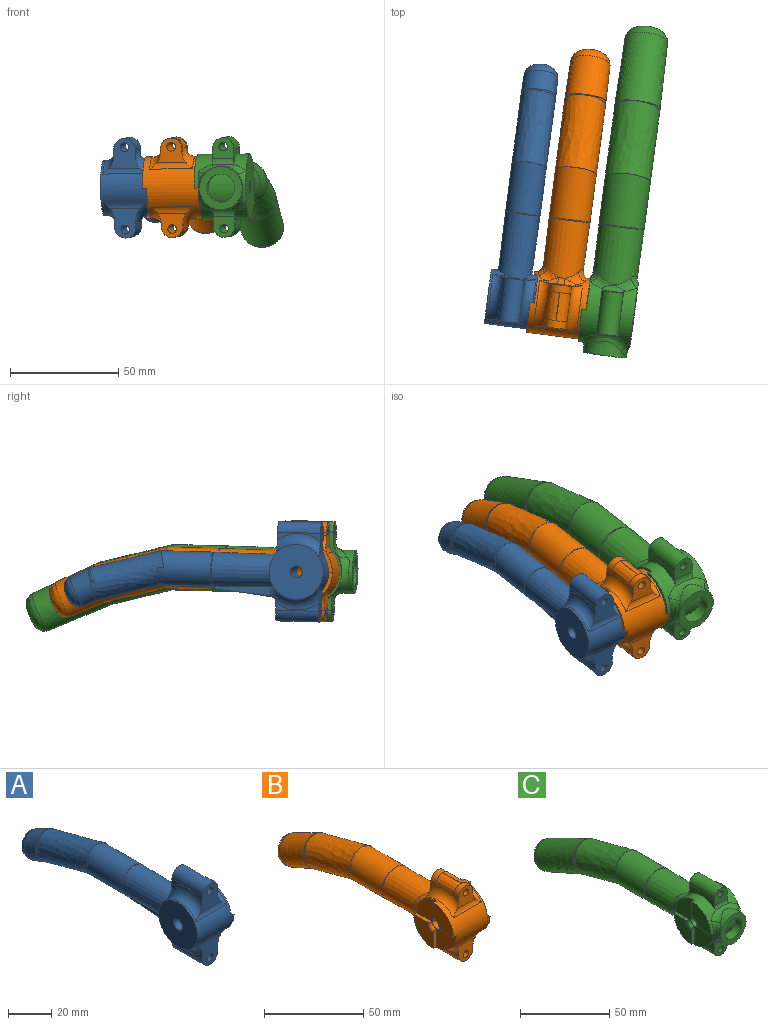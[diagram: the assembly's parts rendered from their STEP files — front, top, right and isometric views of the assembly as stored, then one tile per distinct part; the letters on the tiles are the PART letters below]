
ASSEMBLY  parts=3 mates=2
PART A: 65 faces, bbox 29.9x133.2x48.8 mm
  f0: plane 12.65x12.65mm, normal (1,0,0), area 119.5mm2, adj f1,f9,f11,f12
  f1: plane 9.85x2mm, normal (0,-1,0), area 18.8mm2, adj f0,f2,f8,f12
  f2: plane 12.65x12.65mm, normal (1,0,0), area 107.6mm2, adj f1,f3,f8,f12
  f3: plane 9.85x2mm, normal (0,0,-1), area 18.8mm2, adj f2,f4,f8,f12
  f4: plane 12.65x12.65mm, normal (1,0,0), area 119.5mm2, adj f3,f5,f9,f12
  f5: plane 9.85x2mm, normal (0,1,0), area 18.8mm2, adj f4,f6,f7,f12
  f6: plane 12.65x12.65mm, normal (1,0,0), area 107.6mm2, adj f5,f7,f11,f12
  f7: torus R=4.8mm, axis (1,0,0), area 17.4mm2, adj f5,f6,f9,f11
  f8: torus R=4.8mm, axis (1,0,0), area 17.4mm2, adj f1,f2,f3,f9
  f9: cylinder r=2.8mm len=22mm, axis (1,0,0), area 387mm2, adj f0,f4,f7,f8,f10
  f10: plane 25.3x25.3mm, normal (-1,0,0), area 478.1mm2, adj f9,f12
  f11: plane 9.85x2mm, normal (0,0,1), area 18.8mm2, adj f0,f6,f7,f12
  f12: cylinder r=12.65mm len=25.3mm, axis (-1,0,0), area 626.3mm2, adj f0,f1,f2,f3,f4,f5,f6,f10
  f13: torus R=17.65mm, axis (1,0,0), area 177.5mm2, adj f12,f14,f18,f19,f20,f22
  f14: plane 15.43x14.51mm, normal (0,1,0), area 128.9mm2, adj f13,f15,f16,f17,f19,f21,f22
  f15: plane 20x3.46mm, normal (1,0,0), area 26.9mm2, adj f14,f16,f18,f21
  f16: cylinder r=5mm len=20mm, axis (0,1,0), area 314.2mm2, adj f14,f15,f18,f19
  f17: cylinder r=2mm len=20mm, axis (0,1,0), area 251.3mm2, adj f14,f18
  f18: plane 14.2x13.92mm, normal (0,-1,0), area 120.3mm2, adj f13,f15,f16,f17,f19,f20,f21
  f19: plane 20x3.46mm, normal (-1,0,0), area 26.9mm2, adj f13,f14,f16,f18
  f20: cylinder r=5mm len=20mm, axis (-1,0,0), area 47.2mm2, adj f12,f13,f18,f21
  f21: torus R=17.65mm, axis (1,0,0), area 177.5mm2, adj f12,f14,f15,f18,f20,f22
  f22: cylinder r=3mm len=20mm, axis (-1,0,0), area 27.8mm2, adj f12,f13,f14,f21,f43
  f23: cylinder r=3mm len=7.15mm, axis (0,0,-1), area 23.7mm2, adj f12,f24,f25,f32,f35,f36,f37,f43
  f24: plane 3.09x2.1mm, normal (0,1,0), area 2.6mm2, adj f23,f36,f37
  f25: cylinder r=3mm len=10.04mm, axis (-1,0,0), area 32.2mm2, adj f23,f26,f32,f37,f39,f42
  f26: plane 10x8.54mm, normal (0,1,0), area 62.1mm2, adj f25,f27,f29,f30,f31,f37,f39
  f27: plane 20x3.46mm, normal (-1,0,0), area 26.9mm2, adj f26,f28,f29,f39
  f28: plane 13.98x13.7mm, normal (0,-1,0), area 120.3mm2, adj f27,f29,f30,f31,f37,f38,f39
  f29: cylinder r=5mm len=20mm, axis (0,-1,0), area 314.2mm2, adj f26,f27,f28,f30
  f30: plane 20x3.46mm, normal (1,0,0), area 26.9mm2, adj f26,f28,f29,f37
  f31: cylinder r=2mm len=20mm, axis (0,1,0), area 251.3mm2, adj f26,f28
  f32: plane 27.33x5.03mm, normal (0,0.09,-1), area 137.3mm2, adj f23,f25,f33,f34,f35,f42
  f33: plane 6.3x3.44mm, normal (0,0.53,0.85), area 10.1mm2, adj f32,f34,f35,f43
  f34: plane 27.05x4.1mm, normal (-1,0,0), area 71.9mm2, adj f32,f33,f42,f43
  f35: plane 27.05x4.1mm, normal (1,0,0), area 71.9mm2, adj f23,f32,f33,f43
  f36: cylinder r=3mm len=6.17mm, axis (-1,0,0), area 7.3mm2, adj f12,f23,f24,f37
  f37: torus R=17.65mm, axis (1,0,0), area 176.7mm2, adj f12,f23,f24,f25,f26,f28,f30,f36
  f38: cylinder r=5mm len=20mm, axis (-1,0,0), area 47.2mm2, adj f12,f28,f37,f39
  f39: torus R=17.65mm, axis (1,0,0), area 176.7mm2, adj f12,f25,f26,f27,f28,f38,f40,f41
  f40: plane 3.1x2.11mm, normal (0,1,0), area 2.6mm2, adj f39,f41,f42
  f41: cylinder r=3mm len=6.17mm, axis (-1,0,0), area 7.3mm2, adj f12,f39,f40,f42
  f42: cylinder r=3mm len=7.15mm, axis (0,0,1), area 23.7mm2, adj f12,f25,f32,f34,f39,f40,f41,f43
  f43: cone r=8mm half-angle=0.5deg, axis (0,1,0), area 1269.4mm2, adj f12,f22,f23,f33,f34,f35,f42,f44
  f44: revolved ~16x16mm, area 43.9mm2, adj f43,f45
  f45: cylinder r=8mm len=24.78mm, axis (0,-1,0), area 1203.2mm2, adj f44,f46,f53,f54
  f46: extruded ~37.81x23.99mm, area 1582mm2, adj f45,f47,f48,f49,f53,f54
  f47: bspline ~16x7.05mm, area 0mm2, adj f46,f48
  f48: plane 18.67x9.72mm, normal (0,-0.91,0.42), area 2.5mm2, adj f46,f47
  f49: plane 18.66x17.58mm, normal (0,0.97,-0.26), area 1.8mm2, adj f46,f50
  f50: bspline ~17.04x15.92mm, area 394.6mm2, adj f49,f51
  f51: bspline ~15.65x15.49mm, area 282.7mm2, adj f50,f52
  f52: plane 5.65x4.42mm, normal (0,0.91,-0.42), area 21.5mm2, adj f51
  f53: plane 16x7.84mm, normal (0,-0.97,0.26), area 5.9mm2, adj f45,f46,f54
  f54: extruded ~3x1.15mm, area 0.6mm2, adj f45,f46,f53
  f55: cylinder r=12.65mm len=7.98mm, axis (-1,0,0), area 15.7mm2, adj f59,f61,f62,f63
  f56: plane 8x7.11mm, normal (0,0.91,-0.42), area 49.3mm2, adj f58
  f57: plane 10.36x6.76mm, normal (0,0.97,-0.26), area 8.2mm2, adj f58,f59
  f58: extruded ~34.57x16.19mm, area 786.2mm2, adj f56,f57,f59,f60
  f59: cylinder r=4mm len=52.79mm, axis (0,1,0), area 1145.8mm2, adj f55,f57,f58,f60,f61,f62,f63,f64
  f60: cylinder r=4mm len=3mm, axis (0,1,0), area 0.6mm2, adj f58,f59
  f61: plane 5x2.16mm, normal (0,0.42,-0.91), area 8.7mm2, adj f55,f59,f62,f63
  f62: plane 18.53x6.25mm, normal (1,0,0), area 82.9mm2, adj f55,f59,f61,f64
  f63: plane 18.53x6.25mm, normal (-1,0,0), area 82.9mm2, adj f55,f59,f61,f64
  f64: plane 15.59x10.81mm, normal (0,-0.53,-0.85), area 70.2mm2, adj f59,f62,f63
PART B: 89 faces, bbox 30.3x142.9x53.6 mm
  f0: plane 14.71x14.71mm, normal (-1,0,0), area 151.1mm2, adj f1,f75,f76,f77,f78
  f1: cylinder r=14.15mm len=28.3mm, axis (-1,0,0), area 732mm2, adj f0,f2,f34,f35,f36,f37,f38,f40
  f2: cylinder r=5mm len=20mm, axis (-1,0,0), area 55.5mm2, adj f1,f3,f34,f74
  f3: plane 13.2x11.23mm, normal (0,-1,0), area 92mm2, adj f2,f4,f5,f32,f33,f34,f74
  f4: plane 3.46x1.67mm, normal (-1,0,0), area 2.6mm2, adj f3,f5,f74
  f5: cylinder r=5mm len=10mm, axis (0,1,0), area 54.4mm2, adj f3,f4,f6,f31,f32
  f6: bspline ~18.4x5.66mm, area 97.7mm2, adj f5,f7,f8,f74
  f7: plane 13.07x0.13mm, normal (0,0,1), area 0.9mm2, adj f6,f31
  f8: cylinder r=5mm len=10mm, axis (0,1,0), area 54.4mm2, adj f6,f9,f10,f11,f31
  f9: plane 3.46x1.67mm, normal (1,0,0), area 2.6mm2, adj f8,f11,f34
  f10: plane 3.46x1.67mm, normal (-1,0,0), area 2.6mm2, adj f8,f11,f74
  f11: plane 14.55x11.95mm, normal (0,1,0), area 93.7mm2, adj f8,f9,f10,f12,f13,f30,f33,f34
  f12: bspline ~6.48x3.42mm, area 18.4mm2, adj f11,f13,f72,f73
  f13: torus R=12.26mm, axis (0,1,0), area 15.9mm2, adj f11,f12,f14,f30
  f14: cone r=9.5mm half-angle=0.5deg, axis (0,1,0), area 1289.9mm2, adj f13,f15,f17,f18,f19,f36,f37,f48
  f15: plane 28.43x6.7mm, normal (1,0,0), area 56.4mm2, adj f14,f16,f18,f48,f63
  f16: cylinder r=3mm len=5mm, axis (-1,0,0), area 21.6mm2, adj f15,f17,f18,f63
  f17: plane 28.43x6.69mm, normal (-1,0,0), area 56.4mm2, adj f14,f16,f18,f63,f64
  f18: plane 25.69x5mm, normal (0,0.13,-0.99), area 121.5mm2, adj f14,f15,f16,f17
  f19: revolved ~19x19mm, area 52.1mm2, adj f14,f20
  f20: cylinder r=9.5mm len=24.78mm, axis (0,-1,0), area 1436.2mm2, adj f19,f21,f28,f29
  f21: extruded ~38.56x26.79mm, area 1900.1mm2, adj f20,f22,f23,f24,f28,f29
  f22: bspline ~19x8.34mm, area 0mm2, adj f21,f23
  f23: plane 19.26x8.6mm, normal (0,-0.91,0.42), area 2.3mm2, adj f21,f22
  f24: plane 22.16x20.88mm, normal (0,0.97,-0.26), area 2.2mm2, adj f21,f25
  f25: bspline ~23.93x23.7mm, area 1035.6mm2, adj f24,f26
  f26: bspline ~18.31x17.75mm, area 345.6mm2, adj f25,f27
  f27: plane 8.3x6.69mm, normal (0,0.91,-0.42), area 48mm2, adj f26
  f28: plane 19x9.24mm, normal (0,-0.97,0.26), area 5.4mm2, adj f20,f21,f29
  f29: extruded ~3x1.15mm, area 0.6mm2, adj f20,f21,f28
  f30: bspline ~6.35x3.35mm, area 18.4mm2, adj f11,f13,f35,f36
  f31: bspline ~18.4x5.66mm, area 97.7mm2, adj f5,f7,f8,f34
  f32: plane 3.46x1.67mm, normal (1,0,0), area 2.6mm2, adj f3,f5,f34
  f33: cylinder r=2mm len=20mm, axis (0,1,0), area 251.3mm2, adj f3,f11
  f34: torus R=19.15mm, axis (1,0,0), area 174.3mm2, adj f1,f2,f3,f9,f11,f31,f32,f35
  f35: cylinder r=3mm len=3.08mm, axis (-1,0,0), area 3.6mm2, adj f1,f11,f30,f34
  f36: bspline ~11.34x7.93mm, area 33.4mm2, adj f1,f14,f30,f37
  f37: bspline ~15.66x6.2mm, area 62.8mm2, adj f1,f14,f36,f47,f48
  f38: plane 11.35x2mm, normal (0,0,-1), area 21.8mm2, adj f1,f39,f40,f47
  f39: torus R=4.8mm, axis (1,0,0), area 17.4mm2, adj f38,f40,f41,f76
  f40: plane 14.15x14.15mm, normal (1,0,0), area 139.2mm2, adj f1,f38,f39,f41
  f41: plane 11.35x2mm, normal (0,-1,0), area 21.8mm2, adj f1,f39,f40,f42
  f42: plane 14.15x14.15mm, normal (1,0,0), area 151.1mm2, adj f1,f41,f43,f76
  f43: plane 11.35x2mm, normal (0,0,1), area 21.8mm2, adj f1,f42,f44,f45
  f44: torus R=4.8mm, axis (1,0,0), area 17.4mm2, adj f43,f45,f46,f76
  f45: plane 14.15x14.15mm, normal (1,0,0), area 139.2mm2, adj f1,f43,f44,f46
  f46: plane 11.35x2mm, normal (0,1,0), area 21.8mm2, adj f1,f44,f45,f47
  f47: plane 14.71x14.71mm, normal (1,0,0), area 151.1mm2, adj f1,f37,f38,f46,f76
  f48: bspline ~9.3x7.24mm, area 39.3mm2, adj f1,f14,f15,f37,f63
  f49: torus R=19.15mm, axis (1,0,0), area 170.7mm2, adj f1,f50,f57,f58,f59,f61,f63
  f50: plane 3.46x1.67mm, normal (1,0,0), area 2.6mm2, adj f49,f51,f59
  f51: cylinder r=5mm len=10mm, axis (0,-1,0), area 54.4mm2, adj f50,f52,f56,f57,f59
  f52: bspline ~18.4x5.66mm, area 97.7mm2, adj f51,f53,f54,f62
  f53: plane 13.07x0.13mm, normal (0,0,-1), area 0.9mm2, adj f52,f57
  f54: cylinder r=5mm len=10mm, axis (0,-1,0), area 54.4mm2, adj f52,f55,f57,f58,f63
  f55: plane 3.46x1.67mm, normal (-1,0,0), area 2.6mm2, adj f54,f62,f63
  f56: plane 3.46x1.67mm, normal (-1,0,0), area 2.6mm2, adj f51,f59,f62
  f57: bspline ~18.4x5.66mm, area 97.7mm2, adj f49,f51,f53,f54
  f58: plane 3.46x1.67mm, normal (1,0,0), area 2.6mm2, adj f49,f54,f63
  f59: plane 13.2x11.23mm, normal (0,-1,0), area 92mm2, adj f49,f50,f51,f56,f60,f61,f62
  f60: cylinder r=2mm len=20mm, axis (0,1,0), area 251.3mm2, adj f59,f63
  f61: cylinder r=5mm len=20mm, axis (-1,0,0), area 55.5mm2, adj f1,f49,f59,f62
  f62: torus R=19.15mm, axis (1,0,0), area 170.7mm2, adj f1,f52,f55,f56,f59,f61,f63
  f63: plane 20.93x13.92mm, normal (0,1,0), area 93.4mm2, adj f1,f15,f16,f17,f48,f49,f54,f55
  f64: bspline ~11.02x8.01mm, area 39.3mm2, adj f1,f14,f17,f63,f78
  f65: plane 14.15x14.15mm, normal (-1,0,0), area 139.2mm2, adj f1,f66,f67,f77
  f66: torus R=4.8mm, axis (-1,0,0), area 17.4mm2, adj f65,f67,f76,f77
  f67: plane 11.35x2mm, normal (0,-1,0), area 21.8mm2, adj f1,f65,f66,f68
  f68: plane 14.15x14.15mm, normal (-1,0,0), area 151.1mm2, adj f1,f67,f69,f76
  f69: plane 11.35x2mm, normal (0,0,-1), area 21.8mm2, adj f1,f68,f70,f71
  f70: torus R=4.8mm, axis (-1,0,0), area 17.4mm2, adj f69,f71,f75,f76
  f71: plane 14.15x14.15mm, normal (-1,0,0), area 139.2mm2, adj f1,f69,f70,f75
  f72: bspline ~11.05x8mm, area 33.4mm2, adj f1,f12,f14,f78
  f73: cylinder r=3mm len=3.08mm, axis (-1,0,0), area 3.6mm2, adj f1,f11,f12,f74
  f74: torus R=19.15mm, axis (1,0,0), area 174.3mm2, adj f1,f2,f3,f4,f6,f10,f11,f73
  f75: plane 11.35x2mm, normal (0,1,0), area 21.8mm2, adj f0,f1,f70,f71
  f76: cylinder r=2.8mm len=22mm, axis (1,0,0), area 387mm2, adj f0,f39,f42,f44,f47,f66,f68,f70
  f77: plane 11.35x2mm, normal (0,0,1), area 21.8mm2, adj f0,f1,f65,f66
  f78: bspline ~15.66x6.2mm, area 62.8mm2, adj f0,f1,f14,f64,f72
  f79: cylinder r=5.5mm len=52.02mm, axis (0,1,0), area 1595.4mm2, adj f80,f81,f83,f84,f85,f86,f87,f88
  f80: cylinder r=5.5mm len=3mm, axis (0,1,0), area 0.6mm2, adj f79,f84
  f81: cylinder r=14.15mm len=10.99mm, axis (-1,0,0), area 47.6mm2, adj f79,f85,f86,f87
  f82: plane 11x9.78mm, normal (0,0.91,-0.42), area 93.2mm2, adj f84
  f83: plane 11x5.9mm, normal (0,0.97,-0.26), area 12.1mm2, adj f79,f84
  f84: extruded ~35.57x19.06mm, area 1085.7mm2, adj f79,f80,f82,f83
  f85: plane 5.13x3.74mm, normal (0,0.42,-0.91), area 18.9mm2, adj f79,f81,f86,f87,f88
  f86: plane 20.35x9.8mm, normal (1,0,0), area 115mm2, adj f79,f81,f85,f88
  f87: plane 20.35x9.8mm, normal (-1,0,0), area 115mm2, adj f79,f81,f85,f88
  f88: plane 17.41x10.93mm, normal (0,-0.53,-0.85), area 99.4mm2, adj f79,f85,f86,f87
PART C: 74 faces, bbox 28.8x158x59.5 mm
  f0: cylinder r=15.15mm len=25.94mm, axis (-1,0,0), area 164.5mm2, adj f1,f61,f62,f63
  f1: bspline ~23.08x7.77mm, area 88.7mm2, adj f0,f2,f8,f9,f55,f56,f60,f61
  f2: cylinder r=5mm len=10mm, axis (-1,0,0), area 29.8mm2, adj f1,f3,f8,f61
  f3: plane 10x9.55mm, normal (0,-1,0), area 72.2mm2, adj f2,f4,f7,f8,f61
  f4: cylinder r=5mm len=20mm, axis (0,1,0), area 314.2mm2, adj f3,f5,f8,f61
  f5: plane 10.28x10mm, normal (0,1,0), area 76.2mm2, adj f4,f6,f7,f8,f61
  f6: bspline ~11.09x3.13mm, area 38.4mm2, adj f5,f8,f61,f62
  f7: cylinder r=2mm len=20mm, axis (0,1,0), area 251.3mm2, adj f3,f5
  f8: plane 22.35x7.79mm, normal (-1,0,0), area 81.5mm2, adj f1,f2,f3,f4,f5,f6,f9,f62
  f9: cylinder r=15.15mm len=28.02mm, axis (-1,0,0), area 212.1mm2, adj f1,f8,f10,f18,f19,f20,f55,f62
  f10: plane 12.35x2mm, normal (0,0,-1), area 23.8mm2, adj f9,f11,f18,f20
  f11: torus R=4.8mm, axis (-1,0,0), area 17.4mm2, adj f10,f12,f18,f19
  f12: cylinder r=2.8mm len=22mm, axis (1,0,0), area 387mm2, adj f11,f13,f20,f63
  f13: torus R=4.8mm, axis (-1,0,0), area 17.4mm2, adj f12,f14,f16,f17
  f14: plane 14.15x14.15mm, normal (-1,0,0), area 139.2mm2, adj f13,f15,f16,f17
  f15: cylinder r=14.15mm len=14.15mm, axis (1,0,0), area 44.5mm2, adj f14,f16,f17,f20
  f16: plane 11.35x2mm, normal (0,0,1), area 21.8mm2, adj f13,f14,f15,f20
  f17: plane 11.35x2mm, normal (0,-1,0), area 21.8mm2, adj f13,f14,f15,f20
  f18: plane 15.15x15.15mm, normal (-1,0,0), area 162.2mm2, adj f9,f10,f11,f19
  f19: plane 12.35x2mm, normal (0,1,0), area 23.8mm2, adj f9,f11,f18,f20
  f20: plane 31.27x31.27mm, normal (-1,0,0), area 371.2mm2, adj f9,f10,f12,f15,f16,f17,f19,f21
  f21: cylinder r=15.15mm len=25.94mm, axis (-1,0,0), area 164.5mm2, adj f20,f22,f52,f53
  f22: bspline ~22x7.25mm, area 88.7mm2, adj f21,f23,f50,f51,f52,f55,f56,f60
  f23: cylinder r=5mm len=10mm, axis (-1,0,0), area 33mm2, adj f22,f24,f50,f52
  f24: plane 10x9.55mm, normal (0,-1,0), area 72.2mm2, adj f23,f25,f49,f50,f52
  f25: cylinder r=5mm len=20mm, axis (0,-1,0), area 314.2mm2, adj f24,f26,f50,f52
  f26: plane 10x6.81mm, normal (0,1,0), area 44.8mm2, adj f25,f27,f49,f50,f52
  f27: cylinder r=3mm len=10mm, axis (-1,0,0), area 32mm2, adj f26,f28,f46,f47
  f28: plane 23.47x8.74mm, normal (0,0.15,-0.99), area 93.9mm2, adj f27,f29,f44,f45,f46,f47
  f29: cone r=10.5mm half-angle=0.5deg, axis (0,1,0), area 1465.2mm2, adj f28,f30,f32,f33,f44,f45,f53,f54
  f30: bspline ~8.77x6.96mm, area 34mm2, adj f29,f31,f32,f45,f46,f50,f51
  f31: bspline ~3.4x2.93mm, area 3.8mm2, adj f30,f46,f50
  f32: bspline ~17.62x5.87mm, area 61.2mm2, adj f29,f30,f62,f63
  f33: revolved ~21x21mm, area 57.6mm2, adj f29,f34
  f34: cylinder r=10.5mm len=24.78mm, axis (0,-1,0), area 1592.8mm2, adj f33,f35,f42,f43
  f35: extruded ~39.06x28.65mm, area 2097.7mm2, adj f34,f36,f37,f38,f42,f43
  f36: bspline ~21x9.2mm, area 0mm2, adj f35,f37
  f37: plane 21.29x9.49mm, normal (0,-0.91,0.42), area 2mm2, adj f35,f36
  f38: plane 24.49x23.08mm, normal (0,0.97,-0.26), area 2.5mm2, adj f35,f39
  f39: bspline ~38.21x31.52mm, area 2067.3mm2, adj f38,f40
  f40: bspline ~19.79x19mm, area 380.4mm2, adj f39,f41
  f41: plane 9.78x7.94mm, normal (0,0.91,-0.42), area 67.1mm2, adj f40
  f42: plane 21x10.17mm, normal (0,-0.97,0.26), area 4.9mm2, adj f34,f35,f43
  f43: extruded ~3x1.15mm, area 0.6mm2, adj f34,f35,f42
  f44: plane 19.37x3.2mm, normal (-1,0,0), area 31mm2, adj f28,f29,f47,f53
  f45: plane 19.37x3.2mm, normal (1,0,0), area 31mm2, adj f28,f29,f30,f46
  f46: cylinder r=3mm len=6.18mm, axis (0,0,-1), area 13.7mm2, adj f27,f28,f30,f31,f45,f50
  f47: cylinder r=3mm len=6.18mm, axis (0,0,-1), area 13.7mm2, adj f27,f28,f44,f48,f52,f53
  f48: bspline ~3.37x2.93mm, area 3.8mm2, adj f47,f52,f53
  f49: cylinder r=2mm len=20mm, axis (0,1,0), area 251.3mm2, adj f24,f26
  f50: plane 22.35x7.79mm, normal (1,0,0), area 81.5mm2, adj f22,f23,f24,f25,f26,f30,f31,f46
  f51: cylinder r=15.15mm len=25.94mm, axis (-1,0,0), area 164.5mm2, adj f22,f30,f50,f63
  f52: plane 22.35x7.78mm, normal (-1,0,0), area 81.5mm2, adj f21,f22,f23,f24,f25,f26,f47,f48
  f53: bspline ~11.12x7.83mm, area 34mm2, adj f21,f29,f44,f47,f48,f52,f54
  f54: bspline ~17.62x5.87mm, area 61.2mm2, adj f20,f29,f53,f62
  f55: bspline ~16.67x5.79mm, area 62mm2, adj f1,f9,f20,f22,f56
  f56: cone r=10.5mm half-angle=0.5deg, axis (0,1,0), area 236.7mm2, adj f1,f22,f55,f57,f60
  f57: plane 19.95x19.95mm, normal (0,-1,0), area 179.9mm2, adj f56,f58
  f58: cylinder r=6.5mm len=13mm, axis (0,1,0), area 255.8mm2, adj f57,f59
  f59: cylinder r=15.15mm len=13mm, axis (-1,0,0), area 136mm2, adj f58
  f60: bspline ~16.67x5.79mm, area 62mm2, adj f1,f22,f56,f63
  f61: plane 22.35x7.78mm, normal (1,0,0), area 81.5mm2, adj f0,f1,f2,f3,f4,f5,f6,f62
  f62: bspline ~23.95x7.99mm, area 72mm2, adj f0,f6,f8,f9,f29,f32,f54,f61
  f63: plane 31.27x31.27mm, normal (1,0,0), area 696.4mm2, adj f0,f12,f32,f51,f60
  f64: cylinder r=15.15mm len=13mm, axis (-1,0,0), area 76.6mm2, adj f68,f70,f71,f72
  f65: plane 13x11.56mm, normal (0,0.91,-0.42), area 130.2mm2, adj f67
  f66: plane 13x6.9mm, normal (0,0.97,-0.26), area 15mm2, adj f67,f68
  f67: extruded ~36.23x20.97mm, area 1286.7mm2, adj f65,f66,f68,f69
  f68: cylinder r=6.5mm len=51.14mm, axis (0,1,0), area 1868.5mm2, adj f64,f66,f67,f69,f71,f72,f73
  f69: cylinder r=6.5mm len=3mm, axis (0,1,0), area 0.6mm2, adj f67,f68
  f70: plane 5x2.69mm, normal (0,0.42,-0.91), area 14.8mm2, adj f64,f71,f72,f73
  f71: plane 21.47x11.33mm, normal (1,0,0), area 128.8mm2, adj f64,f68,f70,f73
  f72: plane 21.47x11.33mm, normal (-1,0,0), area 128.8mm2, adj f64,f68,f70,f73
  f73: plane 20.5x13.42mm, normal (0,-0.53,-0.85), area 109.9mm2, adj f68,f70,f71,f72
PLACE A rot(axis=(0.19,-0.07,-0.98),7.6deg) t=(40.32,-32.15,-37.67)mm
PLACE B rot(axis=(0.19,-0.07,-0.98),7.6deg) t=(61.93,-34.99,-37.51)mm
PLACE C rot(axis=(0.19,-0.07,-0.98),7.6deg) t=(85.93,-38.14,-37.32)mm
MATE cylindrical B.f1 <-> C.f0  axis (0.99,-0.13,0.01) through (67.63,-76.12,-38.48)mm
MATE fastened A.f7 <-> C.f0  axis (0.99,-0.13,0.01) through (46.03,-73.28,-38.65)mm
